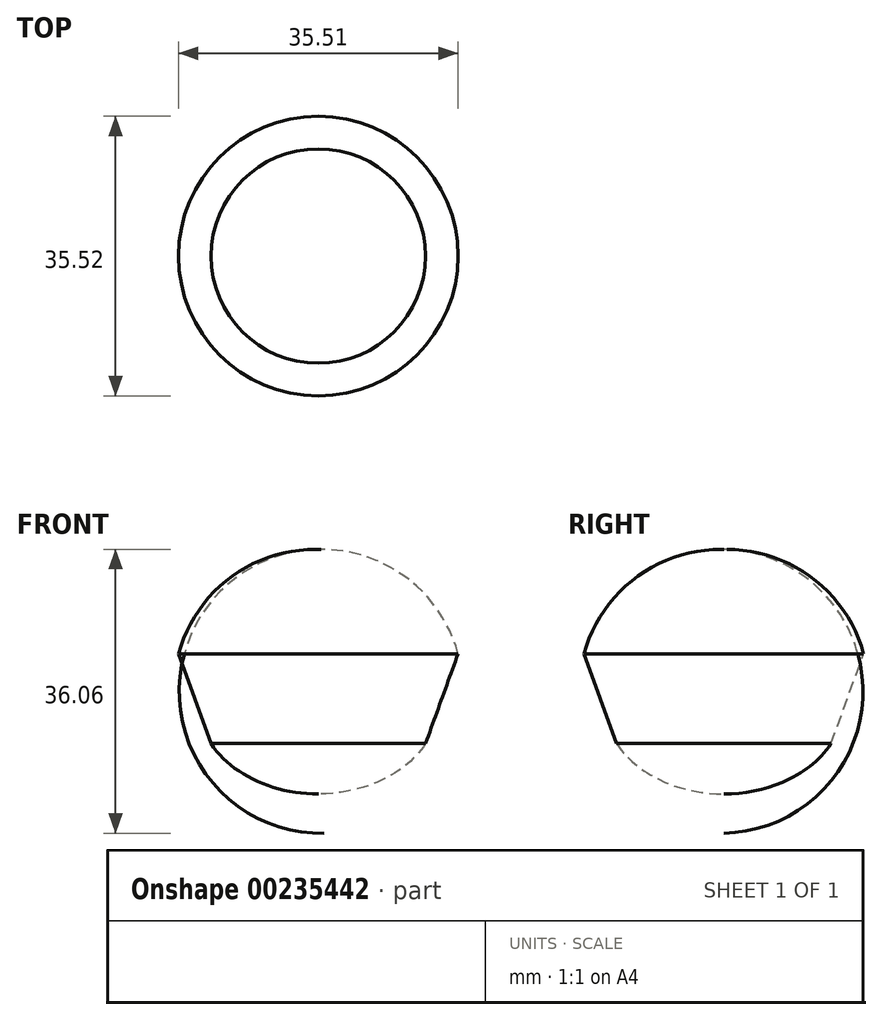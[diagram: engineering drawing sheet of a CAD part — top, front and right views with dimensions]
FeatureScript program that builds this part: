
annotation { "Feature Type Name" : "Feature", "Feature Type Description" : "" }
export const myFeature = defineFeature(function(context is Context, id is Id, definition is map)
    precondition{}
    {
        {
            var Q0;
            Q0=qCreatedBy(makeId("Front.planeOp"),FACE);
            var sketch = newSketch(context, id + "F0", { "sketchPlane" : qUnion([Q0])});
            skLineSegment(sketch, "E0", {"start": v(-45.01, 23.23) * mm, "end": v(-49.15, 34.64) * mm});
            skLineSegment(sketch, "E1", {"start": v(-16.96, 24.58) * mm, "end": v(-14.66, 32.9) * mm});
            skEllipticalArc(sketch, "E2.trimOffspring", {});
            skArc(sketch, "E3", {"start": v(-14.77, 35.9) * mm, "mid": v(-32.43, 47.9) * mm, "end": v(-49.15, 34.64) * mm});
            skPoint(sketch, "E4.visualSharp", {"position": v(-14.28, 34.29) * mm});
            skArc(sketch, "E4.filletArc", {"start": v(-14.66, 32.9) * mm, "mid": v(-14.49, 34.41) * mm, "end": v(-14.77, 35.9) * mm});
            skLineSegment(sketch, "E5", {"start": v(-31.4, 70.15) * mm, "end": v(-31.4, -5.77) * mm});
            const initialGuessF0  = {"E2.trimOffspring": [-0.03135470300912857, 0.02825246937572956, -1, 0, 0.01519998162984848, 0.011430262105685086, 0.45453580562729107, 2.8149507778012763]};
            skSetInitialGuess(sketch, initialGuessF0);
            skSolve(sketch);
        }
        {
            var Q0;
            {var subQ0=sQuery(id+"F0.wireOp",EDGE,"E0");Q0=makeQuery(id+"F0.imprint","IMPRINT",FACE,{"disambiguationData":[TD([[makeQuery(id+"F0.imprint","IMPRINT",EDGE,{"derivedFrom":subQ0}),-1.0]])]});}
            var Q1;
            Q1=sQuery(id+"F0.wireOp",EDGE,"E5");
            revolve(context, id + "F1", {"entities" : qUnion([Q0]), "axis" : qUnion([Q1]), "revolveType" : RevolveType.FULL});
        }
    });
